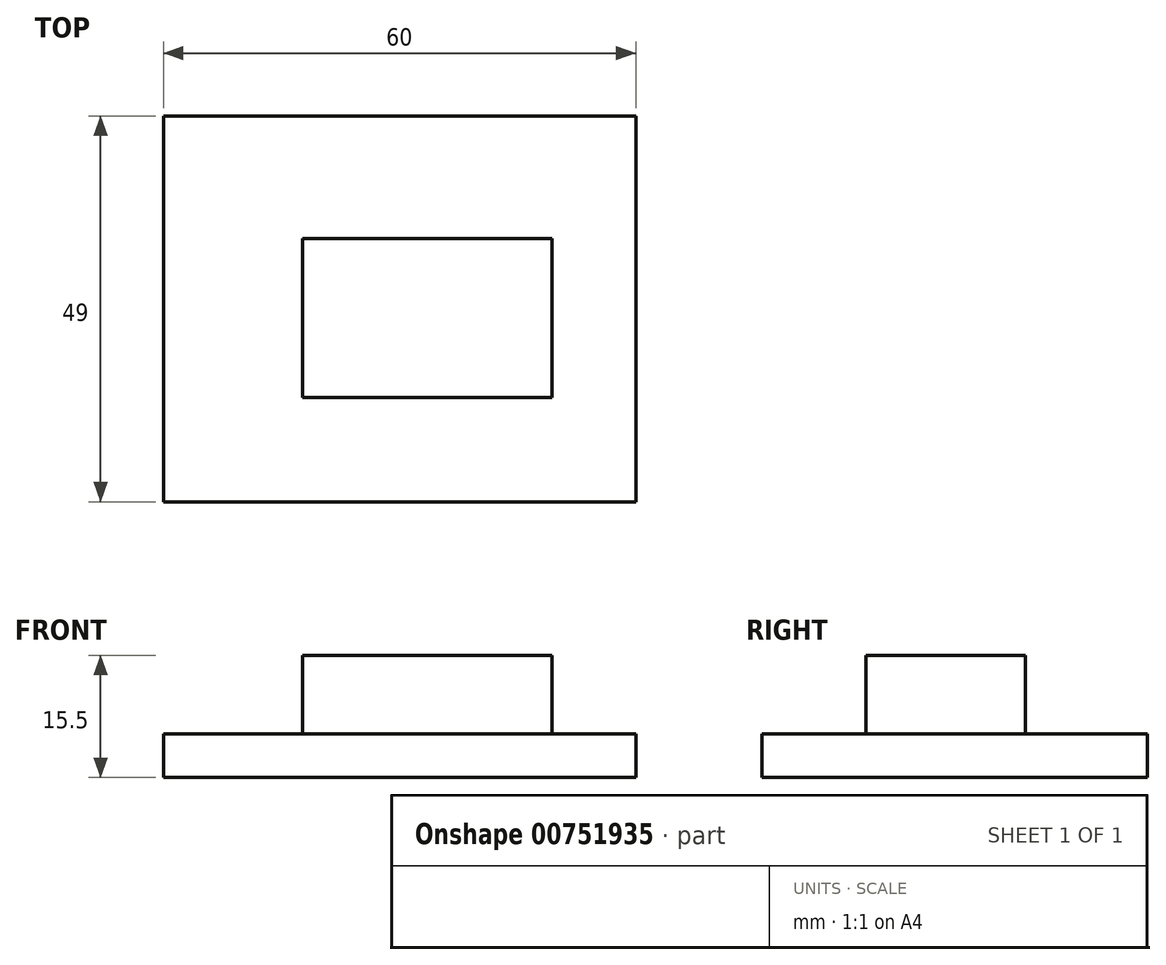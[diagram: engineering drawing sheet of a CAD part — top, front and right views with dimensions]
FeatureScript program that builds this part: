
annotation { "Feature Type Name" : "Feature", "Feature Type Description" : "" }
export const myFeature = defineFeature(function(context is Context, id is Id, definition is map)
    precondition{}
    {
        {
            var Q0;
            Q0=qCreatedBy(makeId("Top.planeOp"),FACE);
            var sketch = newSketch(context, id + "F0", { "sketchPlane" : qUnion([Q0])});
            skLineSegment(sketch, "E0.bottom", {"start": v(-48.38, 43.95) * mm, "end": v(11.62, 43.95) * mm});
            skLineSegment(sketch, "E0.top", {"start": v(-48.38, -5.05) * mm, "end": v(11.62, -5.05) * mm});
            skLineSegment(sketch, "E0.left", {"start": v(-48.38, 43.95) * mm, "end": v(-48.38, -5.05) * mm});
            skLineSegment(sketch, "E0.right", {"start": v(11.62, 43.95) * mm, "end": v(11.62, -5.05) * mm});
            skSolve(sketch);
        }
        {
            var Q0;
            Q0=makeQuery(id+"F0.imprint","IMPRINT",FACE,{"disambiguationData":[TD([[makeQuery(id+"F0.imprint","IMPRINT",EDGE,{"derivedFrom":sQuery(id+"F0.wireOp",EDGE,"E0.bottom")}),-1.0]])]});
            extrude(context, id + "F1", {"entities" : qUnion([Q0]), "depth" : 2.5 * mm, "offsetDistance" : 25 * mm});
        }
        {
            var Q0;
            Q0=makeQuery(id+"F1.opExtrude","CAP_FACE",FACE,{"disambiguationData":[OSD([sQuery(id+"F0.wireOp",EDGE,"E0.bottom"),sQuery(id+"F0.wireOp",EDGE,"E0.top"),sQuery(id+"F0.wireOp",EDGE,"E0.left"),sQuery(id+"F0.wireOp",EDGE,"E0.right")])],"isStart":false});
            extrude(context, id + "F2", {"entities" : qUnion([Q0]), "operationType" : NewBodyOperationType.ADD, "depth" : 3 * mm, "offsetDistance" : 25 * mm});
        }
        {
            var Q0;
            Q0=makeQuery(id+"F2.opExtrude","CAP_FACE",FACE,{"disambiguationData":[OSD([sQuery(id+"F0.wireOp",EDGE,"E0.bottom"),sQuery(id+"F0.wireOp",EDGE,"E0.top"),sQuery(id+"F0.wireOp",EDGE,"E0.left"),sQuery(id+"F0.wireOp",EDGE,"E0.right")])],"isStart":false});
            var sketch = newSketch(context, id + "F3", { "sketchPlane" : qUnion([Q0])});
            skLineSegment(sketch, "E1.bottom", {"start": v(-30.72, 28.41) * mm, "end": v(1, 28.41) * mm});
            skLineSegment(sketch, "E1.top", {"start": v(-30.72, 8.21) * mm, "end": v(1, 8.21) * mm});
            skLineSegment(sketch, "E1.left", {"start": v(-30.72, 28.41) * mm, "end": v(-30.72, 8.21) * mm});
            skLineSegment(sketch, "E1.right", {"start": v(1, 28.41) * mm, "end": v(1, 8.21) * mm});
            skSolve(sketch);
        }
        {
            var Q0;
            Q0=makeQuery(id+"F3.imprint","IMPRINT",FACE,{"disambiguationData":[TD([[makeQuery(id+"F3.imprint","IMPRINT",EDGE,{"derivedFrom":sQuery(id+"F3.wireOp",EDGE,"E1.bottom")}),-1.0]])]});
            extrude(context, id + "F4", {"entities" : qUnion([Q0]), "operationType" : NewBodyOperationType.ADD, "depth" : 10 * mm, "offsetDistance" : 25 * mm});
        }
    });
